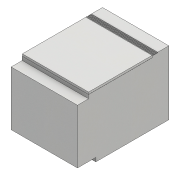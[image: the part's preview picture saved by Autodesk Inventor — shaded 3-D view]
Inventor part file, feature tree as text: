
AUTODESK INVENTOR PART (.ipt)
format: ipt  version: 2018 (Build 220112000, 112)  size: 168,960 bytes
history: native  units: mm
features: extrude x6, sketch x6, projected_geometry x5, pattern_linear x1
ambient origin geometry x8: Origin, YZ Plane, XZ Plane, XY Plane, X Axis, Y Axis, Z Axis, Center Point
bodies: Solid1 (feature_tree), Solid2 (feature_tree)
feature tree (18):
  extrude  "Extrusion1"  Depth=575.0mm
  extrude  "Extrusion2"  Depth=35.0mm
  extrude  "Extrusion3"  Depth=820.0mm TaperAngle=0.0deg
  extrude  "Extrusion4"  Depth=100.0mm
  extrude  "Extrusion5"  Depth=570.0mm
  extrude  "Extrusion6"  Depth=0.5mm
  pattern_linear  "Rectangular Pattern1"  Spacing1=0.5mm  [1 undecoded]
  sketch  "Sketch1"  dims[d0=595.0mm d1=575.0mm]
  sketch  "Sketch2"  dims[d2=820.0mm d3=0.0mm d4=35.0mm]
  projected_geometry  "Projected Loop1"
  sketch  "Sketch3"  dims[d5=165.0mm d6=820.0mm d7=0.0mm]
  projected_geometry  "Projected Loop2"
  sketch  "Sketch4"  dims[d8=52.0mm d9=100.0mm]
  projected_geometry  "Projected Loop3"
  sketch  "Sketch5"  dims[d10=0.0mm d11=0.0mm d12=570.0mm]
  projected_geometry  "Projected Loop4"
  sketch  "Sketch6"  dims[d13=19.0mm d14=0.0mm d15=0.5mm d16=0.5mm d17=19.0mm d18=0.0mm d19=5.0mm d20=5.0mm d21=5.0mm d22=0.0mm d23=50.0mm d25=10.0mm]
  projected_geometry  "Projected Loop5"
note: 1 required parameter value undecoded (feature->parameter linkage not recoverable at this tier; creation-order binding heuristic only, values carry confidence <= 0.55)
